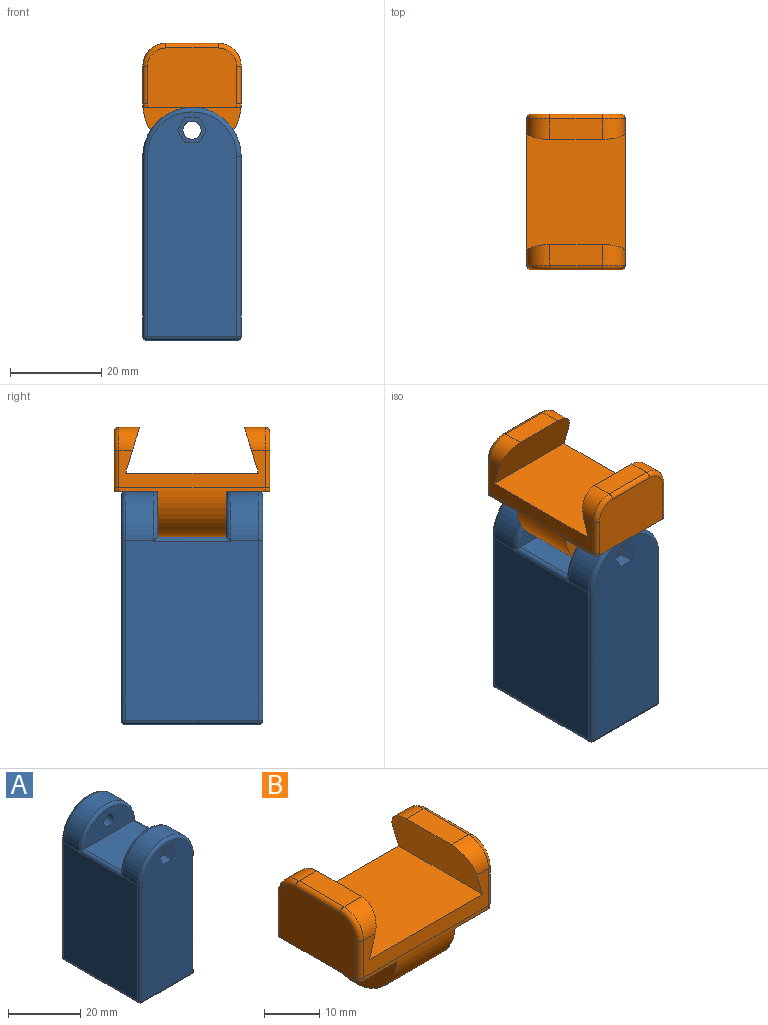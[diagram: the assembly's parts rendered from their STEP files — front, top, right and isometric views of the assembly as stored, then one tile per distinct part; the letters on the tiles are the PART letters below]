
ASSEMBLY  parts=2 mates=1
PART A: 46 faces, bbox 23.3x31x51.9 mm
  f0: plane 19.5x14.5mm, normal (0,0,-1), area 133.4mm2, adj f6,f28,f29,f33
  f1: cylinder r=10.75mm len=21.5mm, axis (0,-1,0), area 202.6mm2, adj f9,f11,f35,f44
  f2: cylinder r=2mm len=5mm, axis (0,-1,0), area 62.8mm2, adj f12,f23
  f3: cylinder r=2mm len=5mm, axis (0,-1,0), area 62.8mm2, adj f13,f16
  f4: plane 19.5x15mm, normal (0,0,1), area 292.5mm2, adj f12,f13,f40,f41,f43,f44
  f5: plane 19.5x14.5mm, normal (0,0,-1), area 133.4mm2, adj f6,f29,f33,f34
  f6: cylinder r=9.75mm len=31mm, axis (0,0,-1), area 1899.1mm2, adj f0,f5,f7
  f7: plane 19.5x19.5mm, normal (0,0,-1), area 298.6mm2, adj f6
  f8: plane 49x19.5mm, normal (0,-1,0), area 888.5mm2, adj f17,f18,f19,f20,f21,f22,f24,f25
  f9: plane 39.25x29mm, normal (1,0,0), area 1134mm2, adj f1,f14,f24,f29,f32,f39,f43,f45
  f10: plane 49x19.5mm, normal (0,1,0), area 886.4mm2, adj f15,f32,f34,f35,f37
  f11: plane 39.25x29mm, normal (-1,0,0), area 1134mm2, adj f1,f14,f27,f33,f37,f38,f41,f42
  f12: plane 19.44x9mm, normal (0,1,0), area 122.1mm2, adj f2,f4,f40
  f13: plane 19.44x9mm, normal (0,-1,0), area 122.1mm2, adj f3,f4,f44
  f14: cylinder r=10.75mm len=21.5mm, axis (0,-1,0), area 202.6mm2, adj f9,f11,f25,f40
  f15: cylinder r=3mm len=6mm, axis (0,1,0), area 56.5mm2, adj f10,f16
  f16: plane 6x6mm, normal (0,1,0), area 15.7mm2, adj f3,f15
  f17: plane 3x2.75mm, normal (0.87,0,0.5), area 9.5mm2, adj f8,f18,f22,f23
  f18: plane 3.18x3mm, normal (0,0,1), area 9.5mm2, adj f8,f17,f19,f23
  f19: plane 3x2.75mm, normal (-0.87,0,0.5), area 9.5mm2, adj f8,f18,f20,f23
  f20: plane 3x2.75mm, normal (-0.87,0,-0.5), area 9.5mm2, adj f8,f19,f21,f23
  f21: plane 3.18x3mm, normal (0,0,-1), area 9.5mm2, adj f8,f20,f22,f23
  f22: plane 3x2.75mm, normal (0.87,0,-0.5), area 9.5mm2, adj f8,f17,f21,f23
  f23: plane 6.35x5.5mm, normal (0,-1,0), area 13.6mm2, adj f2,f17,f18,f19,f20,f21,f22
  f24: cylinder r=1mm len=39.25mm, axis (0,0,1), area 61.7mm2, adj f8,f9,f25,f26
  f25: torus R=9.75mm, axis (0,-1,0), area 51.3mm2, adj f8,f14,f24,f27
  f26: sphere r=1mm, area 1.6mm2, adj f24,f28,f29
  f27: cylinder r=1mm len=39.25mm, axis (0,0,-1), area 61.7mm2, adj f8,f11,f25,f30
  f28: cylinder r=1mm len=19.5mm, axis (1,0,0), area 30.6mm2, adj f0,f8,f26,f30
  f29: cylinder r=1mm len=29mm, axis (0,1,0), area 45.6mm2, adj f0,f5,f9,f26,f31
  f30: sphere r=1mm, area 1.6mm2, adj f27,f28,f33
  f31: sphere r=1mm, area 1.6mm2, adj f29,f32,f34
  f32: cylinder r=1mm len=39.25mm, axis (0,0,-1), area 61.7mm2, adj f9,f10,f31,f35
  f33: cylinder r=1mm len=29mm, axis (0,-1,0), area 45.6mm2, adj f0,f5,f11,f30,f36
  f34: cylinder r=1mm len=19.5mm, axis (-1,0,0), area 30.6mm2, adj f5,f10,f31,f36
  f35: torus R=9.75mm, axis (0,-1,0), area 51.3mm2, adj f1,f10,f32,f37
  f36: sphere r=1mm, area 1.6mm2, adj f33,f34,f37
  f37: cylinder r=1mm len=39.25mm, axis (0,0,1), area 61.7mm2, adj f10,f11,f35,f36
  f38: cylinder r=1mm len=0.25mm, axis (0,0,-1), area 0mm2, adj f11,f40,f41
  f39: cylinder r=1mm len=0.25mm, axis (0,0,-1), area 0mm2, adj f9,f40,f43
  f40: torus R=9.75mm, axis (0,-1,0), area 50mm2, adj f4,f12,f14,f38,f39,f41,f43
  f41: cylinder r=1mm len=17mm, axis (0,-1,0), area 24.7mm2, adj f4,f11,f38,f40,f42,f44
  f42: cylinder r=1mm len=0.25mm, axis (0,0,-1), area 0mm2, adj f11,f41,f44
  f43: cylinder r=1mm len=17mm, axis (0,-1,0), area 24.7mm2, adj f4,f9,f39,f40,f44,f45
  f44: torus R=9.75mm, axis (0,-1,0), area 50mm2, adj f1,f4,f13,f41,f42,f43,f45
  f45: cylinder r=1mm len=0.25mm, axis (0,0,-1), area 0mm2, adj f9,f43,f44
PART B: 33 faces, bbox 34x22.3x24.4 mm
  f0: plane 21.45x9.5mm, normal (0,0,-1), area 203.3mm2, adj f6,f11,f13,f19,f25
  f1: plane 11.5x4.5mm, normal (0,0,1), area 51.7mm2, adj f8,f17,f18,f22
  f2: plane 32x8.25mm, normal (0,1,0), area 126.5mm2, adj f8,f9,f10,f13,f15,f18,f20,f31
  f3: plane 32x8.25mm, normal (0,-1,0), area 126.5mm2, adj f8,f9,f10,f13,f16,f17,f24,f27
  f4: plane 11.5x4.5mm, normal (0,0,1), area 51.8mm2, adj f9,f15,f16,f29
  f5: plane 19.5x13mm, normal (-1,0,0), area 246.6mm2, adj f7,f26,f27,f28,f29,f30,f31,f32
  f6: plane 19.5x13mm, normal (1,0,0), area 246.6mm2, adj f0,f19,f20,f21,f22,f23,f24,f25
  f7: plane 21.45x9.5mm, normal (0,0,-1), area 203.3mm2, adj f5,f12,f13,f26,f32
  f8: plane 21.5x10mm, normal (-0.96,0,-0.29), area 213.3mm2, adj f1,f2,f3,f10,f17,f18
  f9: plane 21.5x10mm, normal (0.96,0,-0.29), area 213.3mm2, adj f2,f3,f4,f10,f15,f16
  f10: plane 29x21.5mm, normal (0,0,1), area 623.5mm2, adj f2,f3,f8,f9
  f11: plane 21.45x10mm, normal (1,0,0), area 152.8mm2, adj f0,f13,f14
  f12: plane 21.45x10mm, normal (-1,0,0), area 152.8mm2, adj f7,f13,f14
  f13: cylinder r=10.75mm len=32mm, axis (1,0,0), area 532.1mm2, adj f0,f2,f3,f7,f11,f12,f19,f25
  f14: cylinder r=2mm len=15mm, axis (-1,0,0), area 188.5mm2, adj f11,f12
  f15: cylinder r=5mm len=5mm, axis (1,0,0), area 31.1mm2, adj f2,f4,f9,f30
  f16: cylinder r=5mm len=5mm, axis (-1,0,0), area 31.1mm2, adj f3,f4,f9,f28
  f17: cylinder r=5mm len=5mm, axis (-1,0,0), area 31.1mm2, adj f1,f3,f8,f23
  f18: cylinder r=5mm len=5mm, axis (1,0,0), area 31.1mm2, adj f1,f2,f8,f21
  f19: torus R=9.75mm, axis (-1,0,0), area 1.2mm2, adj f0,f6,f13,f20
  f20: cylinder r=1mm len=8.25mm, axis (0,0,-1), area 13mm2, adj f2,f6,f19,f21
  f21: torus R=4mm, axis (-1,0,0), area 11.4mm2, adj f6,f18,f20,f22
  f22: cylinder r=1mm len=11.5mm, axis (0,-1,0), area 18.1mm2, adj f1,f6,f21,f23
  f23: torus R=4mm, axis (-1,0,0), area 11.4mm2, adj f6,f17,f22,f24
  f24: cylinder r=1mm len=8.25mm, axis (0,0,1), area 13mm2, adj f3,f6,f23,f25
  f25: torus R=9.75mm, axis (-1,0,0), area 1.2mm2, adj f0,f6,f13,f24
  f26: torus R=9.75mm, axis (-1,0,0), area 1.2mm2, adj f5,f7,f13,f27
  f27: cylinder r=1mm len=8.25mm, axis (0,0,-1), area 13mm2, adj f3,f5,f26,f28
  f28: torus R=4mm, axis (-1,0,0), area 11.4mm2, adj f5,f16,f27,f29
  f29: cylinder r=1mm len=11.5mm, axis (0,1,0), area 18.1mm2, adj f4,f5,f28,f30
  f30: torus R=4mm, axis (-1,0,0), area 11.4mm2, adj f5,f15,f29,f31
  f31: cylinder r=1mm len=8.25mm, axis (0,0,1), area 13mm2, adj f2,f5,f30,f32
  f32: torus R=9.75mm, axis (-1,0,0), area 1.2mm2, adj f5,f7,f13,f31
PLACE A rot(axis=(0,0,-1),0deg) t=(-16.01,7.78,3.12)mm
PLACE B rot(axis=(0,0,1),90deg) t=(-16.01,7.78,23.12)mm
MATE revolute A.f2 <-> B.f14  axis (0,-1,0) through (-16.01,0.28,49.12)mm
